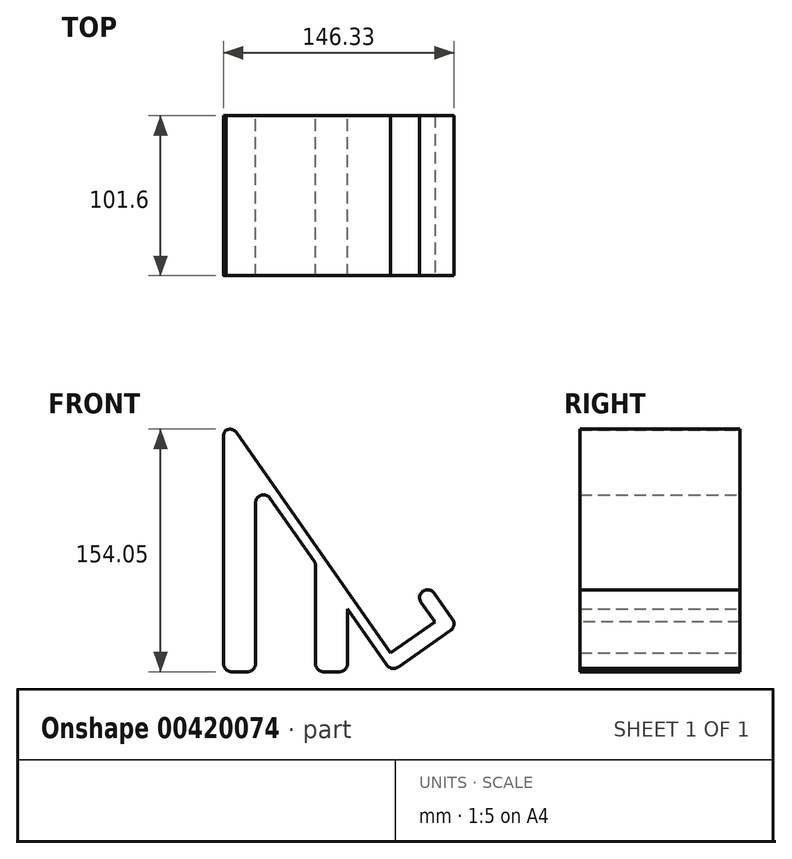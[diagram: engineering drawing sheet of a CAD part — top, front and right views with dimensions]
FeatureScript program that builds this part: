
annotation { "Feature Type Name" : "Feature", "Feature Type Description" : "" }
export const myFeature = defineFeature(function(context is Context, id is Id, definition is map)
    precondition{}
    {
        {
            var Q0;
            Q0=qCreatedBy(makeId("Front.planeOp"),FACE);
            var sketch = newSketch(context, id + "F0", { "sketchPlane" : qUnion([Q0])});
            skPoint(sketch, "E0.start.orphan", {"position": v(-59.33, -55.81) * mm});
            skPoint(sketch, "E1.start.orphan", {"position": v(-59.33, 20.12) * mm});
            skPoint(sketch, "E2.start.orphan", {"position": v(-103.17, -55.81) * mm});
            skLineSegment(sketch, "E3", {"start": v(-21.43, 93.97) * mm, "end": v(85.29, -58.43) * mm});
            skPoint(sketch, "E4.start.orphan", {"position": v(85.29, 87.57) * mm});
            skLineSegment(sketch, "E5", {"start": v(57.31, -58.43) * mm, "end": v(37, -58.43) * mm});
            skLineSegment(sketch, "E6.top", {"start": v(37, -58.43) * mm, "end": v(57.31, -58.43) * mm});
            skLineSegment(sketch, "E6.left", {"start": v(37, 10.54) * mm, "end": v(37, -58.43) * mm});
            skLineSegment(sketch, "E6.right", {"start": v(57.31, -18.48) * mm, "end": v(57.31, -58.43) * mm});
            skLineSegment(sketch, "E7.top", {"start": v(-21.43, -58.43) * mm, "end": v(-1.1, -58.43) * mm});
            skLineSegment(sketch, "E7.left", {"start": v(-21.43, 93.97) * mm, "end": v(-21.43, -58.43) * mm});
            skLineSegment(sketch, "E7.right", {"start": v(-1.1, 64.95) * mm, "end": v(-1.1, -58.43) * mm});
            skLineSegment(sketch, "E8.trimOffspring", {"start": v(-1.1, -58.43) * mm, "end": v(-21.43, -58.43) * mm});
            skLineSegment(sketch, "E9", {"start": v(-21.43, 93.97) * mm, "end": v(166, 93.97) * mm, "construction": true});
            skSolve(sketch);
        }
        {
            var Q0;
            Q0=qSketchRegion(id+"F0",true);
            extrude(context, id + "F1", {"entities" : qUnion([Q0]), "depth" : 101.6 * mm});
        }
        {
            var Q0;
            {var subQ0=sQuery(id+"F0.wireOp",EDGE,"E3");Q0=makeQuery(id+"F1.opExtrude","SWEPT_FACE",FACE,{"disambiguationData":[OSD([subQ0]),TDD([makeQuery(id+"F0.imprint","IMPRINT",EDGE,{"disambiguationData":[TD([[makeQuery(id+"F0.imprint","INTERSECT",VERTEX,{"derivedFrom":[subQ0,sQuery(id+"F0.wireOp",EDGE,"E7.left")]}),-1.0]])],"derivedFrom":subQ0})])]});}
            var sketch = newSketch(context, id + "F2", { "sketchPlane" : qUnion([Q0])});
            skLineSegment(sketch, "E10.top", {"start": v(-101.6, -96.78) * mm, "end": v(0, -96.78) * mm});
            skLineSegment(sketch, "E10.left", {"start": v(-101.6, 89.27) * mm, "end": v(-101.6, -96.78) * mm});
            skLineSegment(sketch, "E10.right", {"start": v(0, 38.47) * mm, "end": v(0, -96.78) * mm});
            skLineSegment(sketch, "E11", {"start": v(-101.6, 89.27) * mm, "end": v(-101.6, 89.27) * mm});
            skLineSegment(sketch, "E12", {"start": v(0, 89.27) * mm, "end": v(-101.6, 89.27) * mm});
            skLineSegment(sketch, "E13", {"start": v(0, 38.47) * mm, "end": v(0, 89.27) * mm});
            skSolve(sketch);
        }
        {
            var Q0;
            Q0=qSketchRegion(id+"F2",true);
            extrude(context, id + "F3", {"entities" : qUnion([Q0]), "operationType" : NewBodyOperationType.ADD, "depth" : 6.35 * mm});
        }
        {
            var Q0;
            Q0=makeQuery(id+"F3.opExtrude","CAP_FACE",FACE,{"disambiguationData":[OSD([sQuery(id+"F2.wireOp",EDGE,"E10.top"),sQuery(id+"F2.wireOp",EDGE,"E10.left"),sQuery(id+"F2.wireOp",EDGE,"E10.right"),sQuery(id+"F2.wireOp",EDGE,"E11"),sQuery(id+"F2.wireOp",EDGE,"E12"),sQuery(id+"F2.wireOp",EDGE,"E13")])],"isStart":false});
            var sketch = newSketch(context, id + "F4", { "sketchPlane" : qUnion([Q0])});
            skLineSegment(sketch, "E14.bottom", {"start": v(-101.6, -96.78) * mm, "end": v(0, -96.78) * mm});
            skLineSegment(sketch, "E14.top", {"start": v(-88.9, -86.62) * mm, "end": v(-12.7, -86.62) * mm});
            skLineSegment(sketch, "E14.left", {"start": v(-101.6, -96.78) * mm, "end": v(-101.6, -86.62) * mm});
            skLineSegment(sketch, "E14.right", {"start": v(0, -96.78) * mm, "end": v(0, -86.62) * mm});
            skLineSegment(sketch, "E15.top", {"start": v(-101.6, 20.8) * mm, "end": v(-88.9, 20.8) * mm});
            skLineSegment(sketch, "E15.left", {"start": v(-101.6, -86.62) * mm, "end": v(-101.6, 20.8) * mm});
            skLineSegment(sketch, "E15.right", {"start": v(-88.9, -86.62) * mm, "end": v(-88.9, 20.8) * mm});
            skLineSegment(sketch, "E16.top", {"start": v(0, 0.13) * mm, "end": v(-12.7, 0.13) * mm});
            skLineSegment(sketch, "E16.left", {"start": v(0, -86.62) * mm, "end": v(0, 0.13) * mm});
            skLineSegment(sketch, "E16.right", {"start": v(-12.7, -86.62) * mm, "end": v(-12.7, 0.13) * mm});
            skLineSegment(sketch, "E17", {"start": v(-88.9, -86.62) * mm, "end": v(-101.6, -86.62) * mm});
            skLineSegment(sketch, "E18", {"start": v(-12.7, -86.62) * mm, "end": v(0, -86.62) * mm});
            skSolve(sketch);
        }
        {
            var Q0;
            Q0=makeQuery(id+"F4.imprint","IMPRINT",FACE,{"disambiguationData":[TD([[makeQuery(id+"F4.imprint","IMPRINT",EDGE,{"derivedFrom":sQuery(id+"F4.wireOp",EDGE,"E14.bottom")}),1.0]])]});
            extrude(context, id + "F5", {"entities" : qUnion([Q0]), "operationType" : NewBodyOperationType.ADD, "depth" : 44.45 * mm});
        }
        {
            var Q0;
            Q0=makeQuery(id+"F5.opExtrude","SWEPT_FACE",FACE,{"disambiguationData":[OSD([sQuery(id+"F4.wireOp",EDGE,"E14.top"),sQuery(id+"F4.wireOp",EDGE,"E17"),sQuery(id+"F4.wireOp",EDGE,"E18")])]});
            var sketch = newSketch(context, id + "F6", { "sketchPlane" : qUnion([Q0])});
            skLineSegment(sketch, "E19.bottom", {"start": v(87.15, 0) * mm, "end": v(76.99, 0) * mm});
            skLineSegment(sketch, "E19.top", {"start": v(87.15, -101.6) * mm, "end": v(76.99, -101.6) * mm});
            skLineSegment(sketch, "E19.left", {"start": v(87.15, 0) * mm, "end": v(87.15, -101.6) * mm});
            skLineSegment(sketch, "E19.right", {"start": v(76.99, 0) * mm, "end": v(76.99, -101.6) * mm});
            skSolve(sketch);
        }
        {
            var Q0;
            Q0=qSketchRegion(id+"F6",true);
            extrude(context, id + "F7", {"entities" : qUnion([Q0]), "operationType" : NewBodyOperationType.ADD, "depth" : 20.32 * mm});
        }
        {
            var Q0;
            Q0=makeQuery(id+"F7.opExtrude","CAP_EDGE",EDGE,{"disambiguationData":[OSD([sQuery(id+"F6.wireOp",EDGE,"E19.left")])],"isStart":false});
            var Q1;
            Q1=makeQuery(id+"F5.opExtrude","CAP_EDGE",EDGE,{"disambiguationData":[OSD([sQuery(id+"F4.wireOp",EDGE,"E14.bottom")])],"isStart":false});
            var Q2;
            Q2=makeQuery(id+"F7.opExtrude","CAP_EDGE",EDGE,{"disambiguationData":[OSD([sQuery(id+"F6.wireOp",EDGE,"E19.right")])],"isStart":false});
            var Q3;
            Q3=makeQuery(id+"F3.opExtrude","CAP_EDGE",EDGE,{"disambiguationData":[OSD([sQuery(id+"F2.wireOp",EDGE,"E12")])],"isStart":false});
            var Q4;
            Q4=makeQuery(id+"F3.opExtrude","CAP_EDGE",EDGE,{"disambiguationData":[OSD([sQuery(id+"F2.wireOp",EDGE,"E10.top")])],"isStart":true});
            var Q5;
            Q5=makeQuery(id+"F5.opExtrude","CAP_EDGE",EDGE,{"disambiguationData":[OSD([sQuery(id+"F4.wireOp",EDGE,"E14.top"),sQuery(id+"F4.wireOp",EDGE,"E17"),sQuery(id+"F4.wireOp",EDGE,"E18")])],"isStart":true});
            var Q6;
            Q6=makeQuery(id+"F3.boolean.opBoolean","MERGE",EDGE,{"derivedFrom":[makeQuery(id+"F1.opExtrude","SWEPT_EDGE",EDGE,{"disambiguationData":[OSD([sQuery(id+"F0.wireOp",EDGE,"E3"),sQuery(id+"F0.wireOp",EDGE,"E7.left")])]}),makeQuery(id+"F3.opExtrude","CAP_EDGE",EDGE,{"disambiguationData":[OSD([sQuery(id+"F2.wireOp",EDGE,"E12")])],"isStart":true})]});
            var Q7;
            Q7=makeQuery(id+"F1.opExtrude","SWEPT_EDGE",EDGE,{"disambiguationData":[OSD([sQuery(id+"F0.wireOp",EDGE,"E7.left"),sQuery(id+"F0.wireOp",EDGE,"E8.trimOffspring")])]});
            var Q8;
            Q8=makeQuery(id+"F1.opExtrude","SWEPT_EDGE",EDGE,{"disambiguationData":[OSD([sQuery(id+"F0.wireOp",EDGE,"E7.right"),sQuery(id+"F0.wireOp",EDGE,"E8.trimOffspring")])]});
            var Q9;
            Q9=makeQuery(id+"F1.opExtrude","SWEPT_EDGE",EDGE,{"disambiguationData":[OSD([sQuery(id+"F0.wireOp",EDGE,"E6.top"),sQuery(id+"F0.wireOp",EDGE,"E6.left")])]});
            var Q10;
            Q10=makeQuery(id+"F1.opExtrude","SWEPT_EDGE",EDGE,{"disambiguationData":[OSD([sQuery(id+"F0.wireOp",EDGE,"E6.top"),sQuery(id+"F0.wireOp",EDGE,"E6.right")])]});
            fillet(context, id + "F8", {"entities" : qUnion([Q0, Q1, Q2, Q3, Q4, Q5, Q6, Q7, Q8, Q9, Q10]), "radius" : 5.08 * mm, "tangentPropagation" : true, "allowEdgeOverflow" : false});
        }
        {
            var Q0;
            Q0=makeQuery(id+"F1.opExtrude","SWEPT_BODY",BODY,{"disambiguationData":[OSD([sQuery(id+"F0.wireOp",EDGE,"E3"),sQuery(id+"F0.wireOp",EDGE,"E7.left"),sQuery(id+"F0.wireOp",EDGE,"E7.right"),sQuery(id+"F0.wireOp",EDGE,"E8.trimOffspring")])]});
            transform(context, id + "F9", {"entities" : qUnion([Q0]), "transformType" : TransformType.TRANSLATION_3D, "dx" : 0 * mm, "dy" : 169.42 * mm, "dz" : 0 * mm, "makeCopy" : true});
        }
        {
            var Q0;
            {var subQ0=sQuery(id+"F0.wireOp",EDGE,"E3");Q0=makeQuery(id+"F9.opPattern","COPY",FACE,{"derivedFrom":makeQuery(id+"F7.boolean.opBoolean","MERGE",FACE,{"derivedFrom":[makeQuery(id+"F5.boolean.opBoolean","MERGE",FACE,{"derivedFrom":[makeQuery(id+"F3.boolean.opBoolean","MERGE",FACE,{"derivedFrom":[makeQuery(id+"F1.opExtrude","CAP_FACE",FACE,{"disambiguationData":[OSD([subQ0,sQuery(id+"F0.wireOp",EDGE,"E7.left"),sQuery(id+"F0.wireOp",EDGE,"E7.right"),sQuery(id+"F0.wireOp",EDGE,"E8.trimOffspring")])],"isStart":false}),makeQuery(id+"F1.opExtrude","CAP_FACE",FACE,{"disambiguationData":[OSD([subQ0,sQuery(id+"F0.wireOp",EDGE,"E6.top"),sQuery(id+"F0.wireOp",EDGE,"E6.left"),sQuery(id+"F0.wireOp",EDGE,"E6.right")])],"isStart":false}),makeQuery(id+"F3.opExtrude","SWEPT_FACE",FACE,{"disambiguationData":[OSD([sQuery(id+"F2.wireOp",EDGE,"E10.left")])]})]}),makeQuery(id+"F5.opExtrude","SWEPT_FACE",FACE,{"disambiguationData":[OSD([sQuery(id+"F4.wireOp",EDGE,"E14.left")])]})]}),makeQuery(id+"F7.opExtrude","SWEPT_FACE",FACE,{"disambiguationData":[OSD([sQuery(id+"F6.wireOp",EDGE,"E19.top")])]})]}),"instanceName":"1"});}
            var sketch = newSketch(context, id + "F10", { "sketchPlane" : qUnion([Q0])});
            skLineSegment(sketch, "E20.bottom", {"start": v(-64.76, 118.4) * mm, "end": v(186.28, 118.4) * mm});
            skLineSegment(sketch, "E20.top", {"start": v(-64.76, -85.54) * mm, "end": v(186.28, -85.54) * mm});
            skLineSegment(sketch, "E20.left", {"start": v(-64.76, 118.4) * mm, "end": v(-64.76, -85.54) * mm});
            skLineSegment(sketch, "E20.right", {"start": v(186.28, 118.4) * mm, "end": v(186.28, -85.54) * mm});
            skSolve(sketch);
        }
        {
            var Q0;
            Q0 = qSketchRegion(id + "F10", true);
            extrude(context, id + "F11", {"entities" : qUnion([Q0]), "operationType" : NewBodyOperationType.REMOVE, "oppositeDirection" : true, "depth" : 160.78 * mm});
        }
    });
